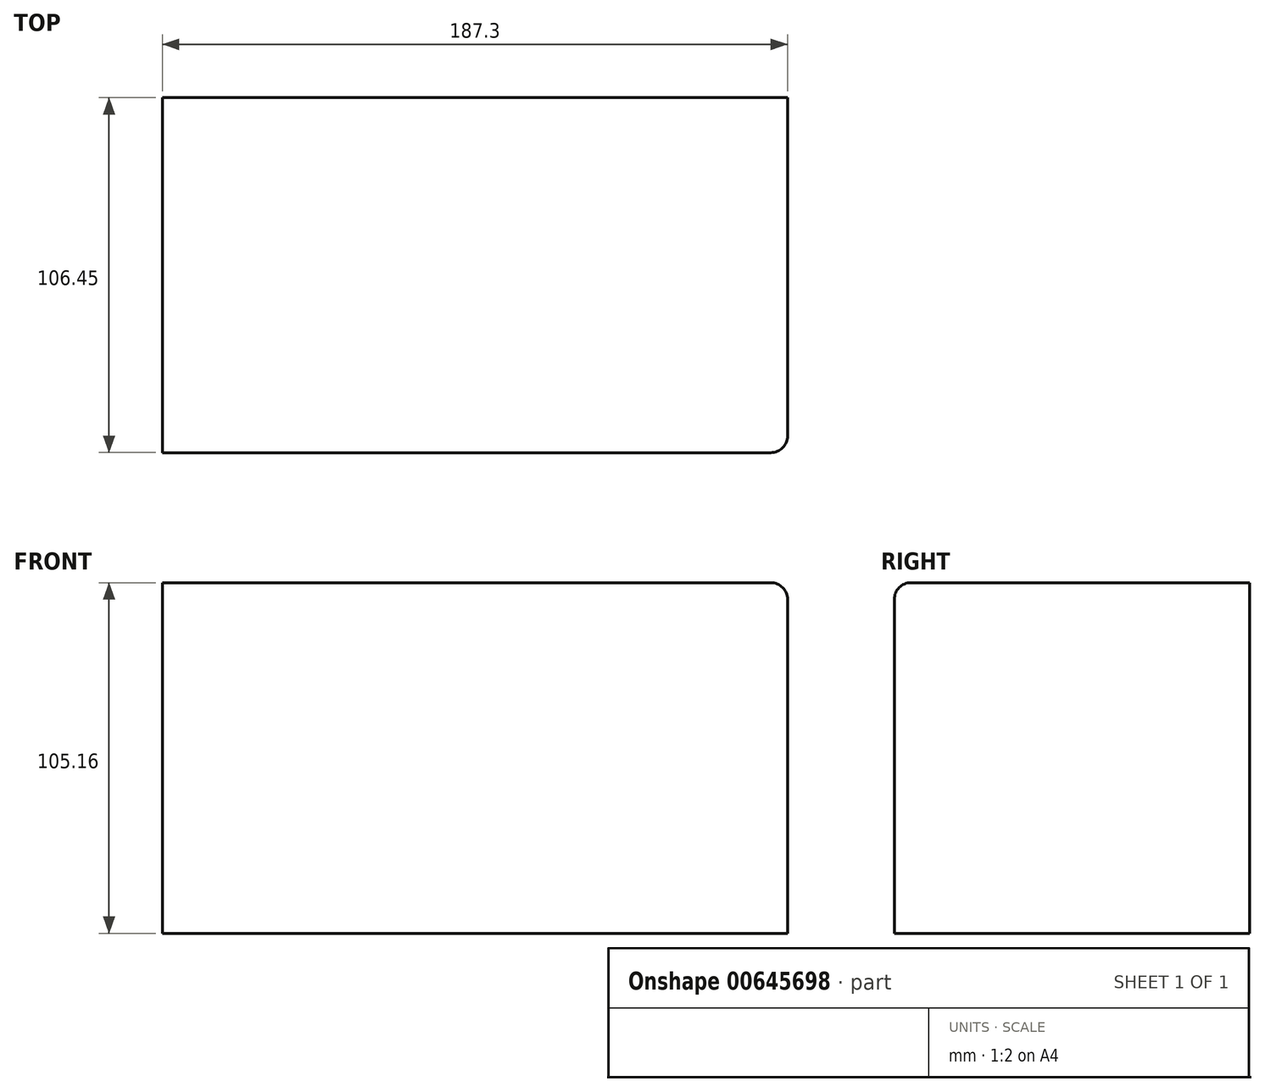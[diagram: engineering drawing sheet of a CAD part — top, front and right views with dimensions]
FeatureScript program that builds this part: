
annotation { "Feature Type Name" : "Feature", "Feature Type Description" : "" }
export const myFeature = defineFeature(function(context is Context, id is Id, definition is map)
    precondition{}
    {
        {
            var Q0;
            Q0=qCreatedBy(makeId("Top.planeOp"),FACE);
            var sketch = newSketch(context, id + "F0", { "sketchPlane" : qUnion([Q0])});
            skLineSegment(sketch, "E0", {"start": v(0, 74.2) * mm, "end": v(137.3, 74.2) * mm});
            skLineSegment(sketch, "E1", {"start": v(137.3, 74.2) * mm, "end": v(137.3, -32.24) * mm});
            skLineSegment(sketch, "E2", {"start": v(137.3, -32.24) * mm, "end": v(0, -32.24) * mm});
            skLineSegment(sketch, "E3", {"start": v(0, -32.24) * mm, "end": v(0, 74.2) * mm});
            skSolve(sketch);
        }
        {
            var Q0;
            Q0 = qSketchRegion(id + "F0", true);
            extrude(context, id + "F1", {"entities" : qUnion([Q0]), "depth" : 105.16 * mm, "offsetDistance" : 25.4 * mm});
        }
        {
            var Q0;
            Q0=makeQuery(id+"F1.opExtrude","SWEPT_FACE",FACE,{"disambiguationData":[OSD([sQuery(id+"F0.wireOp",EDGE,"E1")])]});
            extrude(context, id + "F2", {"entities" : qUnion([Q0]), "operationType" : NewBodyOperationType.ADD, "depth" : 50 * mm, "offsetDistance" : 25 * mm});
        }
        {
            var Q0;
            {var subQ0=sQuery(id+"F0.wireOp",EDGE,"E2");var subQ1=sQuery(id+"F0.wireOp",EDGE,"E1");Q0=makeQuery(id+"F2.boolean.opBoolean","MERGE",EDGE,{"derivedFrom":[makeQuery(id+"F1.opExtrude","CAP_EDGE",EDGE,{"disambiguationData":[OSD([subQ0])],"isStart":false}),makeQuery(id+"F2.opExtrude","SWEPT_EDGE",EDGE,{"disambiguationData":[OSD([subQ1,subQ0]),TDD([makeQuery(id+"F1.opExtrude","CAP_VERTEX",VERTEX,{"disambiguationData":[OSD([subQ1,subQ0])],"isStart":false})])]})]});}
            var Q1;
            {var subQ0=sQuery(id+"F0.wireOp",EDGE,"E1");Q1=makeQuery(id+"F2.opExtrude","CAP_EDGE",EDGE,{"disambiguationData":[OSD([subQ0]),TDD([makeQuery(id+"F1.opExtrude","CAP_EDGE",EDGE,{"disambiguationData":[OSD([subQ0])],"isStart":false})])],"isStart":false});}
            var Q2;
            Q2=makeQuery(id+"F2.opExtrude","CAP_EDGE",EDGE,{"disambiguationData":[OSD([sQuery(id+"F0.wireOp",EDGE,"E1"),sQuery(id+"F0.wireOp",EDGE,"E2")])],"isStart":false});
            fillet(context, id + "F3", {"entities" : qUnion([Q0, Q1, Q2]), "radius" : 5 * mm, "tangentPropagation" : true, "allowEdgeOverflow" : false});
        }
    });
